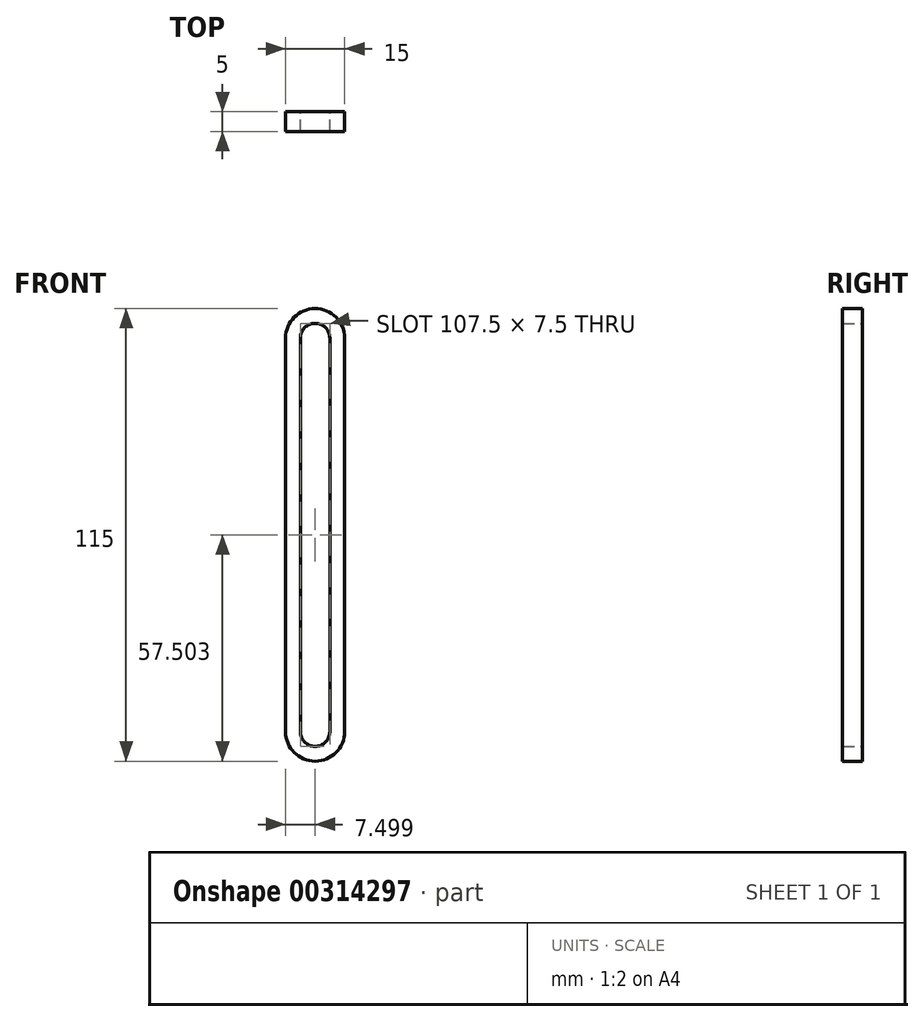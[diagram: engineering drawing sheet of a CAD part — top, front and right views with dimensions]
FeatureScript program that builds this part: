
annotation { "Feature Type Name" : "Feature", "Feature Type Description" : "" }
export const myFeature = defineFeature(function(context is Context, id is Id, definition is map)
    precondition{}
    {
        {
            var Q0;
            Q0=qCreatedBy(makeId("Front.planeOp"),FACE);
            var sketch = newSketch(context, id + "F0", { "sketchPlane" : qUnion([Q0])});
            skLineSegment(sketch, "E0", {"start": v(-53.9, 54.13) * mm, "end": v(-53.9, -45.87) * mm});
            skLineSegment(sketch, "E1", {"start": v(-53.9, 54.13) * mm, "end": v(-38.9, 54.13) * mm});
            skLineSegment(sketch, "E2", {"start": v(-38.9, 54.13) * mm, "end": v(-38.9, -45.87) * mm});
            skLineSegment(sketch, "E3", {"start": v(-53.9, -45.87) * mm, "end": v(-38.9, -45.87) * mm});
            skCircle(sketch, "E4", {"center": v(-46.4, 54.13) * mm, "radius": 7.5 * mm});
            skCircle(sketch, "E5", {"center": v(-46.4, -45.87) * mm, "radius": 7.5 * mm});
            skLineSegment(sketch, "E6", {"start": v(-46.4, 54.13) * mm, "end": v(-38.9, 54.13) * mm});
            skLineSegment(sketch, "E7", {"start": v(-42.65, 54.13) * mm, "end": v(-42.65, -45.87) * mm});
            skLineSegment(sketch, "E8", {"start": v(-53.9, 54.13) * mm, "end": v(-46.4, 54.13) * mm});
            skLineSegment(sketch, "E9", {"start": v(-50.15, 54.13) * mm, "end": v(-50.15, -45.87) * mm});
            skCircle(sketch, "E10", {"center": v(-46.4, 54.13) * mm, "radius": 3.75 * mm});
            skCircle(sketch, "E11", {"center": v(-46.4, -45.87) * mm, "radius": 3.75 * mm});
            skLineSegment(sketch, "E12.bottom", {"start": v(9.25, 0) * mm, "end": v(59.25, 0) * mm});
            skLineSegment(sketch, "E12.top", {"start": v(9.25, 10) * mm, "end": v(59.25, 10) * mm});
            skLineSegment(sketch, "E12.left", {"start": v(9.25, 0) * mm, "end": v(9.25, 10) * mm});
            skLineSegment(sketch, "E12.right", {"start": v(59.25, 0) * mm, "end": v(59.25, 10) * mm});
            skSolve(sketch);
        }
        {
            var Q0;
            {var subQ0=sQuery(id+"F0.wireOp",EDGE,"E0");Q0=makeQuery(id+"F0.imprint","IMPRINT",FACE,{"disambiguationData":[TD([[makeQuery(id+"F0.imprint","IMPRINT",EDGE,{"derivedFrom":subQ0}),1.0]])]});}
            var Q1;
            {var subQ1=sQuery(id+"F0.wireOp",EDGE,"E4");var subQ3=sQuery(id+"F0.wireOp",EDGE,"E9");var subQ4=makeQuery(id+"F0.imprint","INTERSECT",VERTEX,{"derivedFrom":[subQ1,subQ3]});Q1=makeQuery(id+"F0.imprint","IMPRINT",FACE,{"disambiguationData":[TD([[makeQuery(id+"F0.imprint","IMPRINT",EDGE,{"disambiguationData":[TD([[subQ4,1.0]])],"derivedFrom":subQ1}),1.0]])]});}
            var Q2;
            {var subQ0=sQuery(id+"F0.wireOp",EDGE,"E8");var subQ1=sQuery(id+"F0.wireOp",EDGE,"E4");var subQ2=makeQuery(id+"F0.imprint","INTERSECT",VERTEX,{"derivedFrom":[sQuery(id+"F0.wireOp",EDGE,"E0"),subQ1,subQ0]});Q2=makeQuery(id+"F0.imprint","IMPRINT",FACE,{"disambiguationData":[TD([[makeQuery(id+"F0.imprint","IMPRINT",EDGE,{"disambiguationData":[TD([[subQ2,1.0]])],"derivedFrom":subQ1}),1.0]])]});}
            var Q3;
            {var subQ1=sQuery(id+"F0.wireOp",EDGE,"E4");var subQ3=sQuery(id+"F0.wireOp",EDGE,"E7");var subQ4=makeQuery(id+"F0.imprint","INTERSECT",VERTEX,{"derivedFrom":[subQ1,subQ3]});Q3=makeQuery(id+"F0.imprint","IMPRINT",FACE,{"disambiguationData":[TD([[makeQuery(id+"F0.imprint","IMPRINT",EDGE,{"disambiguationData":[TD([[subQ4,-1.0]])],"derivedFrom":subQ1}),1.0]])]});}
            var Q4;
            {var subQ0=sQuery(id+"F0.wireOp",EDGE,"E2");Q4=makeQuery(id+"F0.imprint","IMPRINT",FACE,{"disambiguationData":[TD([[makeQuery(id+"F0.imprint","IMPRINT",EDGE,{"derivedFrom":subQ0}),-1.0]])]});}
            var Q5;
            {var subQ0=sQuery(id+"F0.wireOp",EDGE,"E5");var subQ3=sQuery(id+"F0.wireOp",EDGE,"E7");var subQ5=makeQuery(id+"F0.imprint","INTERSECT",VERTEX,{"derivedFrom":[subQ0,subQ3]});Q5=makeQuery(id+"F0.imprint","IMPRINT",FACE,{"disambiguationData":[TD([[makeQuery(id+"F0.imprint","IMPRINT",EDGE,{"disambiguationData":[TD([[subQ5,1.0]])],"derivedFrom":subQ0}),1.0]])]});}
            var Q6;
            {var subQ0=sQuery(id+"F0.wireOp",EDGE,"E5");var subQ1=sQuery(id+"F0.wireOp",EDGE,"E3");var subQ2=makeQuery(id+"F0.imprint","INTERSECT",VERTEX,{"derivedFrom":[sQuery(id+"F0.wireOp",EDGE,"E0"),subQ1,subQ0]});Q6=makeQuery(id+"F0.imprint","IMPRINT",FACE,{"disambiguationData":[TD([[makeQuery(id+"F0.imprint","IMPRINT",EDGE,{"disambiguationData":[TD([[subQ2,-1.0]])],"derivedFrom":subQ1}),-1.0]])]});}
            var Q7;
            {var subQ0=sQuery(id+"F0.wireOp",EDGE,"E5");var subQ3=sQuery(id+"F0.wireOp",EDGE,"E9");var subQ5=makeQuery(id+"F0.imprint","INTERSECT",VERTEX,{"derivedFrom":[subQ0,subQ3]});Q7=makeQuery(id+"F0.imprint","IMPRINT",FACE,{"disambiguationData":[TD([[makeQuery(id+"F0.imprint","IMPRINT",EDGE,{"disambiguationData":[TD([[subQ5,-1.0]])],"derivedFrom":subQ0}),1.0]])]});}
            extrude(context, id + "F1", {"entities" : qUnion([Q0, Q1, Q2, Q3, Q4, Q5, Q6, Q7]), "depth" : 5 * mm});
        }
    });
